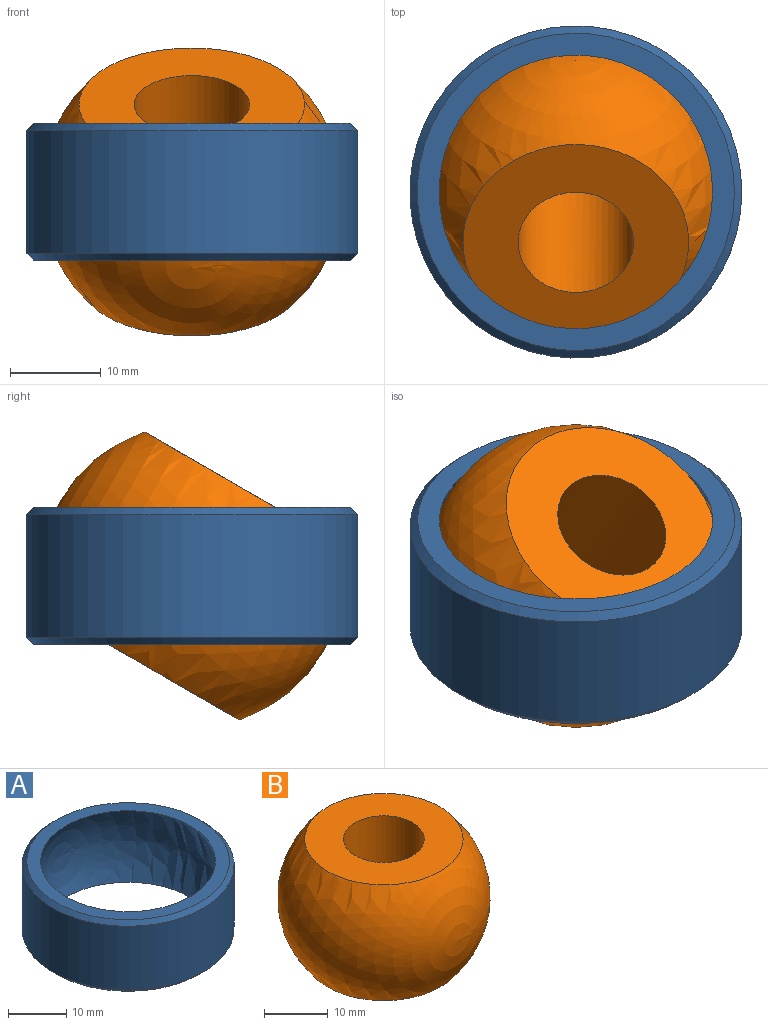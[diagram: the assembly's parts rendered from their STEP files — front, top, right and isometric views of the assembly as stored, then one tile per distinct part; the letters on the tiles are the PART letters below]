
ASSEMBLY  parts=2 mates=1
PART A: 6 faces, bbox 36.5x36.5x33.7 mm
  f0: cylinder r=18.26mm len=36.51mm, axis (0,0,-1), area 1543.5mm2, adj f4,f5
  f1: plane 34.89x34.89mm, normal (0,0,1), area 244.8mm2, adj f3,f4
  f2: plane 34.89x34.89mm, normal (0,0,-1), area 244.8mm2, adj f3,f5
  f3: sphere r=16.83mm, area 1595mm2, adj f1,f2
  f4: cone r=17.44mm half-angle=45deg, axis (0,0,-1), area 128.9mm2, adj f0,f1
  f5: cone r=18.26mm half-angle=45deg, axis (0,0,1), area 128.9mm2, adj f0,f2
PART B: 4 faces, bbox 33.3x33.3x33.3 mm
  f0: sphere r=16.66mm, area 2326.8mm2, adj f1,f2
  f1: plane 24.83x24.83mm, normal (0,0,1), area 357.6mm2, adj f0,f3
  f2: plane 24.83x24.83mm, normal (0,0,-1), area 357.6mm2, adj f0,f3
  f3: cylinder r=6.35mm len=22.23mm, axis (0,0,1), area 886.7mm2, adj f1,f2
PLACE A t=(-6.11,4.56,4.14)mm
PLACE B rot(axis=(1,0,0),30deg) t=(-6.11,4.56,4.14)mm
MATE ball B.f3 <-> A.f0  axis (0,-0.5,0.87) through (-6.11,4.56,4.14)mm
